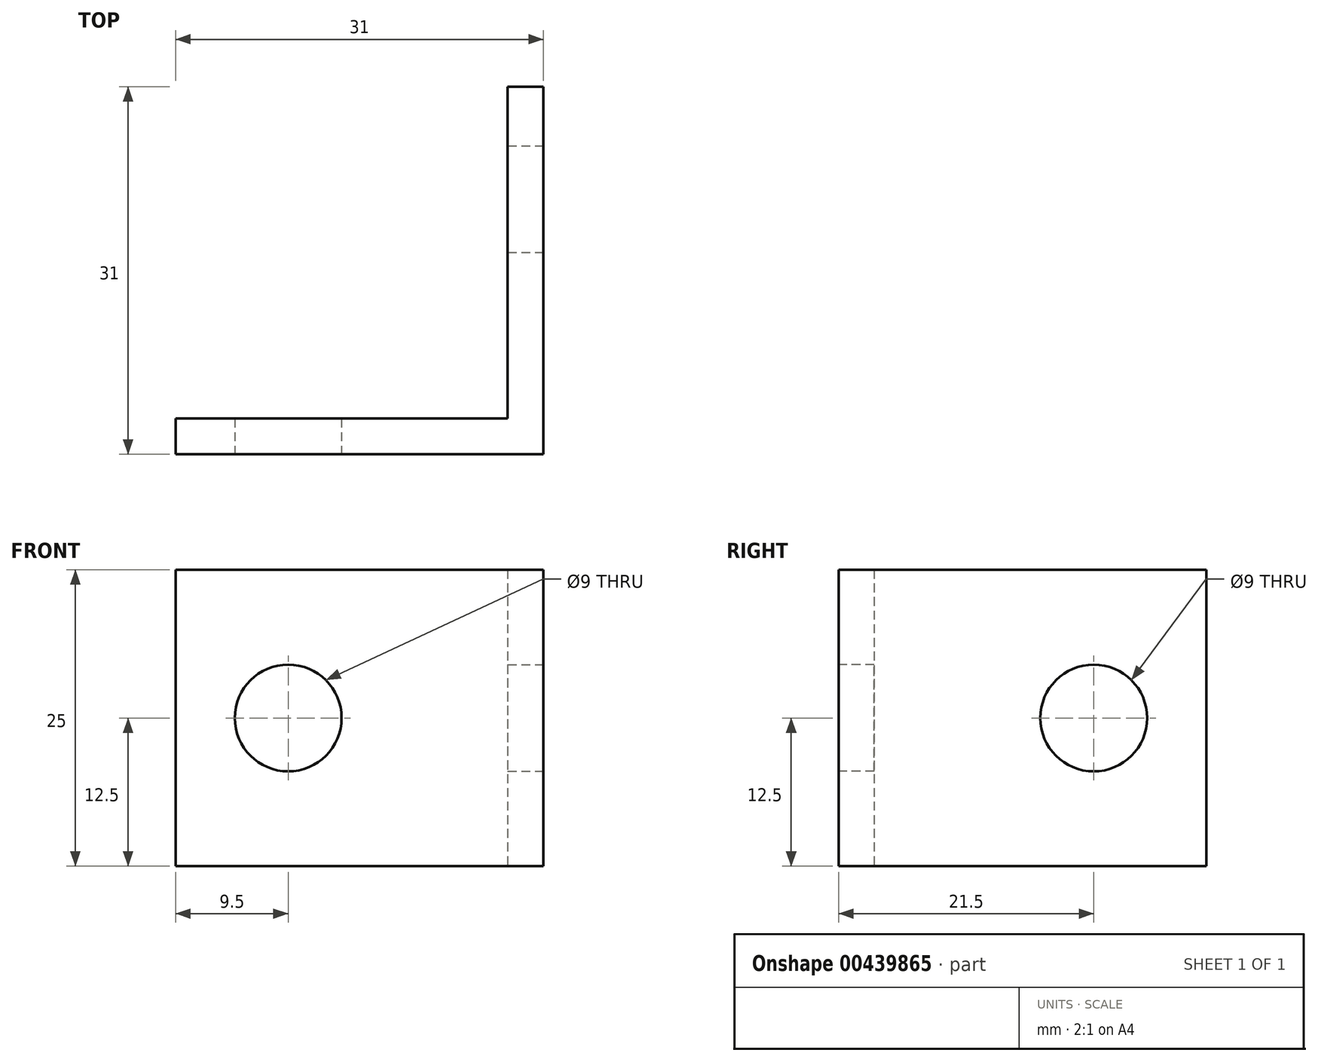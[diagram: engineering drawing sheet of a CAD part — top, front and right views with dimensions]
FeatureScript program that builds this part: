
annotation { "Feature Type Name" : "Feature", "Feature Type Description" : "" }
export const myFeature = defineFeature(function(context is Context, id is Id, definition is map)
    precondition{}
    {
        {
            assignVariable(context, id + "F0", {"name" : "x3", "anyValue" : 25});
        }
        {
            var Q0;
            Q0=qCreatedBy(makeId("Top.planeOp"),FACE);
            var sketch = newSketch(context, id + "F1", { "sketchPlane" : qUnion([Q0])});
            skLineSegment(sketch, "E0", {"start": v(0, 0) * mm, "end": v(-31, 0) * mm});
            skLineSegment(sketch, "E1", {"start": v(0, 0) * mm, "end": v(0, 31) * mm});
            skLineSegment(sketch, "E2.0", {"start": v(-3, 3) * mm, "end": v(-3, 31) * mm});
            skLineSegment(sketch, "E2.1", {"start": v(-3, 3) * mm, "end": v(-31, 3) * mm});
            skLineSegment(sketch, "E3", {"start": v(0, 31) * mm, "end": v(-3, 31) * mm});
            skLineSegment(sketch, "E4", {"start": v(-31, 3) * mm, "end": v(-31, 0) * mm});
            skSolve(sketch);
        }
        {
            var Q0;
            Q0 = qSketchRegion(id + "F1", true);
            extrude(context, id + "F2", {"entities" : qUnion([Q0]), "depth" : (getVariable(context, 'x3')) * mm});
        }
        {
            var Q0;
            Q0=makeQuery(id+"F2.opExtrude","SWEPT_FACE",FACE,{"disambiguationData":[OSD([sQuery(id+"F1.wireOp",EDGE,"E0")])]});
            var sketch = newSketch(context, id + "F3", { "sketchPlane" : qUnion([Q0])});
            skCircle(sketch, "E5", {"center": v(-21.5, 12.5) * mm, "radius": 4.5 * mm});
            skPoint(sketch, "E5.centerSnap0", {"position": v(-15.5, 25) * mm});
            skPoint(sketch, "E5.centerSnap1", {"position": v(-31, 12.5) * mm});
            skSolve(sketch);
        }
        {
            var Q0;
            Q0=makeQuery(id+"F3.imprint","IMPRINT",FACE,{"disambiguationData":[TD([[makeQuery(id+"F3.imprint","IMPRINT",EDGE,{"derivedFrom":sQuery(id+"F3.wireOp",EDGE,"E5")}),1.0]])]});
            extrude(context, id + "F4", {"entities" : qUnion([Q0]), "operationType" : NewBodyOperationType.REMOVE, "endBound" : BoundingType.UP_TO_NEXT, "oppositeDirection" : true, "depth" : 25 * mm});
        }
        {
            var Q0;
            Q0=makeQuery(id+"F2.opExtrude","SWEPT_FACE",FACE,{"disambiguationData":[OSD([sQuery(id+"F1.wireOp",EDGE,"E1")])]});
            var sketch = newSketch(context, id + "F5", { "sketchPlane" : qUnion([Q0])});
            skCircle(sketch, "E6", {"center": v(21.5, 12.5) * mm, "radius": 4.5 * mm});
            skPoint(sketch, "E6.centerSnap0", {"position": v(0, 12.5) * mm});
            skPoint(sketch, "E6.centerSnap1", {"position": v(15.5, 0) * mm});
            skSolve(sketch);
        }
        {
            var Q0;
            Q0=makeQuery(id+"F5.imprint","IMPRINT",FACE,{"disambiguationData":[TD([[makeQuery(id+"F5.imprint","IMPRINT",EDGE,{"derivedFrom":sQuery(id+"F5.wireOp",EDGE,"E6")}),1.0]])]});
            extrude(context, id + "F6", {"entities" : qUnion([Q0]), "operationType" : NewBodyOperationType.REMOVE, "endBound" : BoundingType.UP_TO_NEXT, "oppositeDirection" : true, "depth" : 25 * mm});
        }
    });
